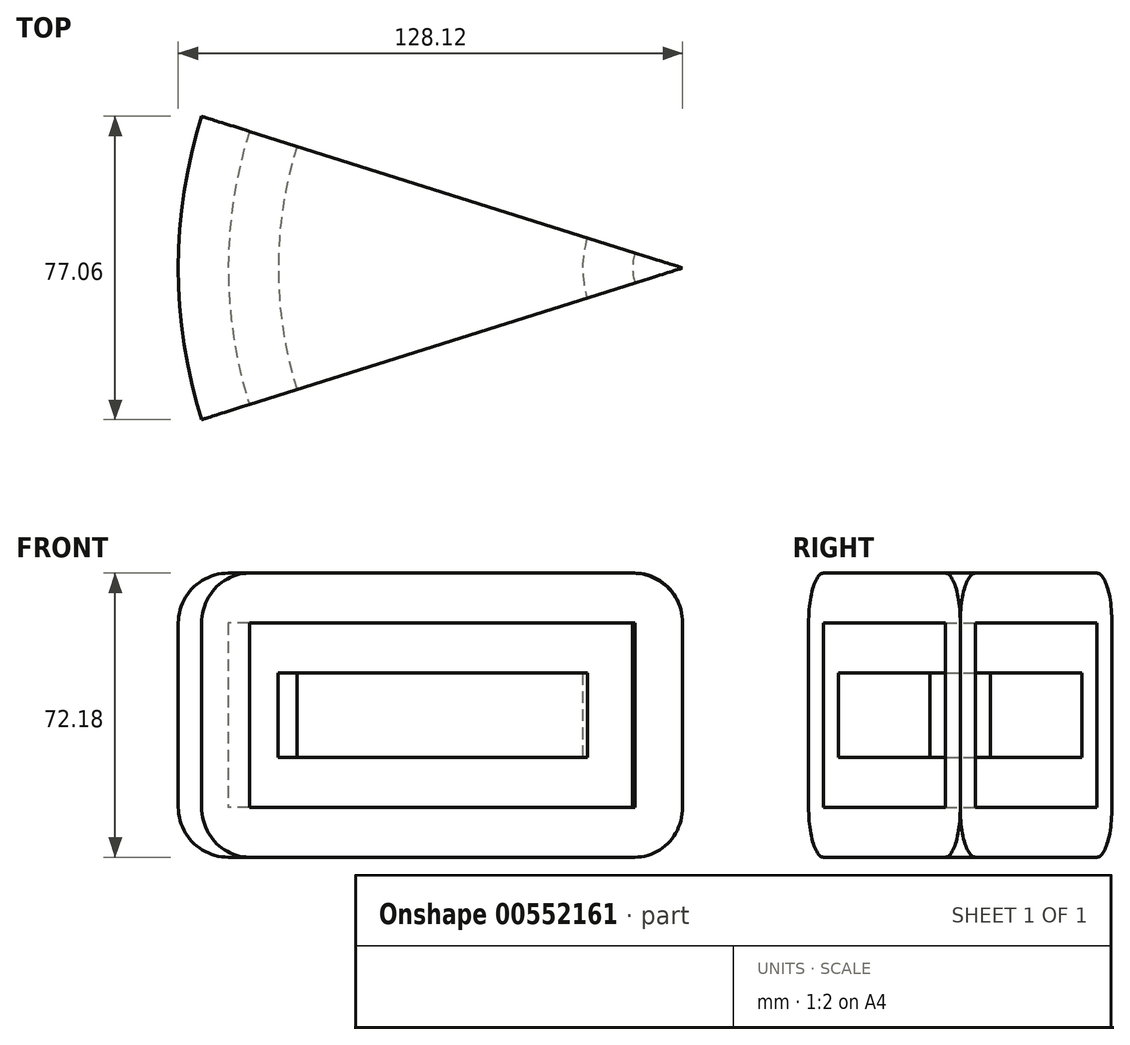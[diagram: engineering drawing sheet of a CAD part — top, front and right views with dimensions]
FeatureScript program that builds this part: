
annotation { "Feature Type Name" : "Feature", "Feature Type Description" : "" }
export const myFeature = defineFeature(function(context is Context, id is Id, definition is map)
    precondition{}
    {
        {
            var Q0;
            Q0=qCreatedBy(makeId("Front.planeOp"),FACE);
            var sketch = newSketch(context, id + "F0", { "sketchPlane" : qUnion([Q0])});
            skLineSegment(sketch, "E0.bottom", {"start": v(51.36, -23.39) * mm, "end": v(-51.36, -23.39) * mm});
            skLineSegment(sketch, "E0.top", {"start": v(51.36, 23.39) * mm, "end": v(-51.36, 23.39) * mm});
            skLineSegment(sketch, "E0.left", {"start": v(51.36, -23.39) * mm, "end": v(51.36, 23.39) * mm});
            skLineSegment(sketch, "E0.right", {"start": v(-51.36, -23.39) * mm, "end": v(-51.36, 23.39) * mm});
            skPoint(sketch, "E0.middle", {"position": v(0, 0) * mm});
            skArc(sketch, "E1.0.startCap", {"start": v(51.36, 36.09) * mm, "mid": v(64.06, 23.39) * mm, "end": v(51.36, 10.69) * mm});
            skArc(sketch, "E1.0.endCap", {"start": v(-51.36, 10.69) * mm, "mid": v(-64.06, 23.39) * mm, "end": v(-51.36, 36.09) * mm});
            skLineSegment(sketch, "E1.0.left", {"start": v(51.36, 10.69) * mm, "end": v(-51.36, 10.69) * mm});
            skLineSegment(sketch, "E1.0.right", {"start": v(51.36, 36.09) * mm, "end": v(-51.36, 36.09) * mm});
            skArc(sketch, "E1.1.startCap", {"start": v(-38.66, -23.39) * mm, "mid": v(-51.36, -36.09) * mm, "end": v(-64.06, -23.39) * mm});
            skArc(sketch, "E1.1.endCap", {"start": v(-64.06, 23.39) * mm, "mid": v(-51.36, 36.09) * mm, "end": v(-38.66, 23.39) * mm});
            skLineSegment(sketch, "E1.1.left", {"start": v(-64.06, -23.39) * mm, "end": v(-64.06, 23.39) * mm});
            skLineSegment(sketch, "E1.1.right", {"start": v(-38.66, -23.39) * mm, "end": v(-38.66, 23.39) * mm});
            skArc(sketch, "E1.2.startCap", {"start": v(64.06, -23.39) * mm, "mid": v(51.36, -36.09) * mm, "end": v(38.66, -23.39) * mm});
            skArc(sketch, "E1.2.endCap", {"start": v(38.66, 23.39) * mm, "mid": v(51.36, 36.09) * mm, "end": v(64.06, 23.39) * mm});
            skLineSegment(sketch, "E1.2.left", {"start": v(38.66, -23.39) * mm, "end": v(38.66, 23.39) * mm});
            skLineSegment(sketch, "E1.2.right", {"start": v(64.06, -23.39) * mm, "end": v(64.06, 23.39) * mm});
            skArc(sketch, "E1.3.startCap", {"start": v(51.36, -10.69) * mm, "mid": v(64.06, -23.39) * mm, "end": v(51.36, -36.09) * mm});
            skArc(sketch, "E1.3.endCap", {"start": v(-51.36, -36.09) * mm, "mid": v(-64.06, -23.39) * mm, "end": v(-51.36, -10.69) * mm});
            skLineSegment(sketch, "E1.3.left", {"start": v(51.36, -36.09) * mm, "end": v(-51.36, -36.09) * mm});
            skLineSegment(sketch, "E1.3.right", {"start": v(51.36, -10.69) * mm, "end": v(-51.36, -10.69) * mm});
            skSolve(sketch);
        }
        {
            var Q0;
            Q0 = qSketchRegion(id + "F0", true);
            var Q1;
            {var subQ0=sQuery(id+"F0.wireOp",EDGE,"E1.2.left");var subQ1=sQuery(id+"F0.wireOp",EDGE,"E1.0.left");var subQ2=makeQuery(id+"F0.imprint","INTERSECT",VERTEX,{"derivedFrom":[subQ1,subQ0]});Q1=makeQuery(id+"F0.imprint","IMPRINT",FACE,{"disambiguationData":[TD([[makeQuery(id+"F0.imprint","IMPRINT",EDGE,{"disambiguationData":[TD([[subQ2,-1.0]])],"derivedFrom":subQ1}),1.0]])]});}
            var Q2;
            Q2=sQuery(id+"F0.wireOp",EDGE,"E1.2.right");
            revolve(context, id + "F1", {"entities" : qUnion([Q0, Q1]), "axis" : qUnion([Q2]), "revolveType" : RevolveType.SYMMETRIC, "angle" : 35 * degree});
        }
    });
